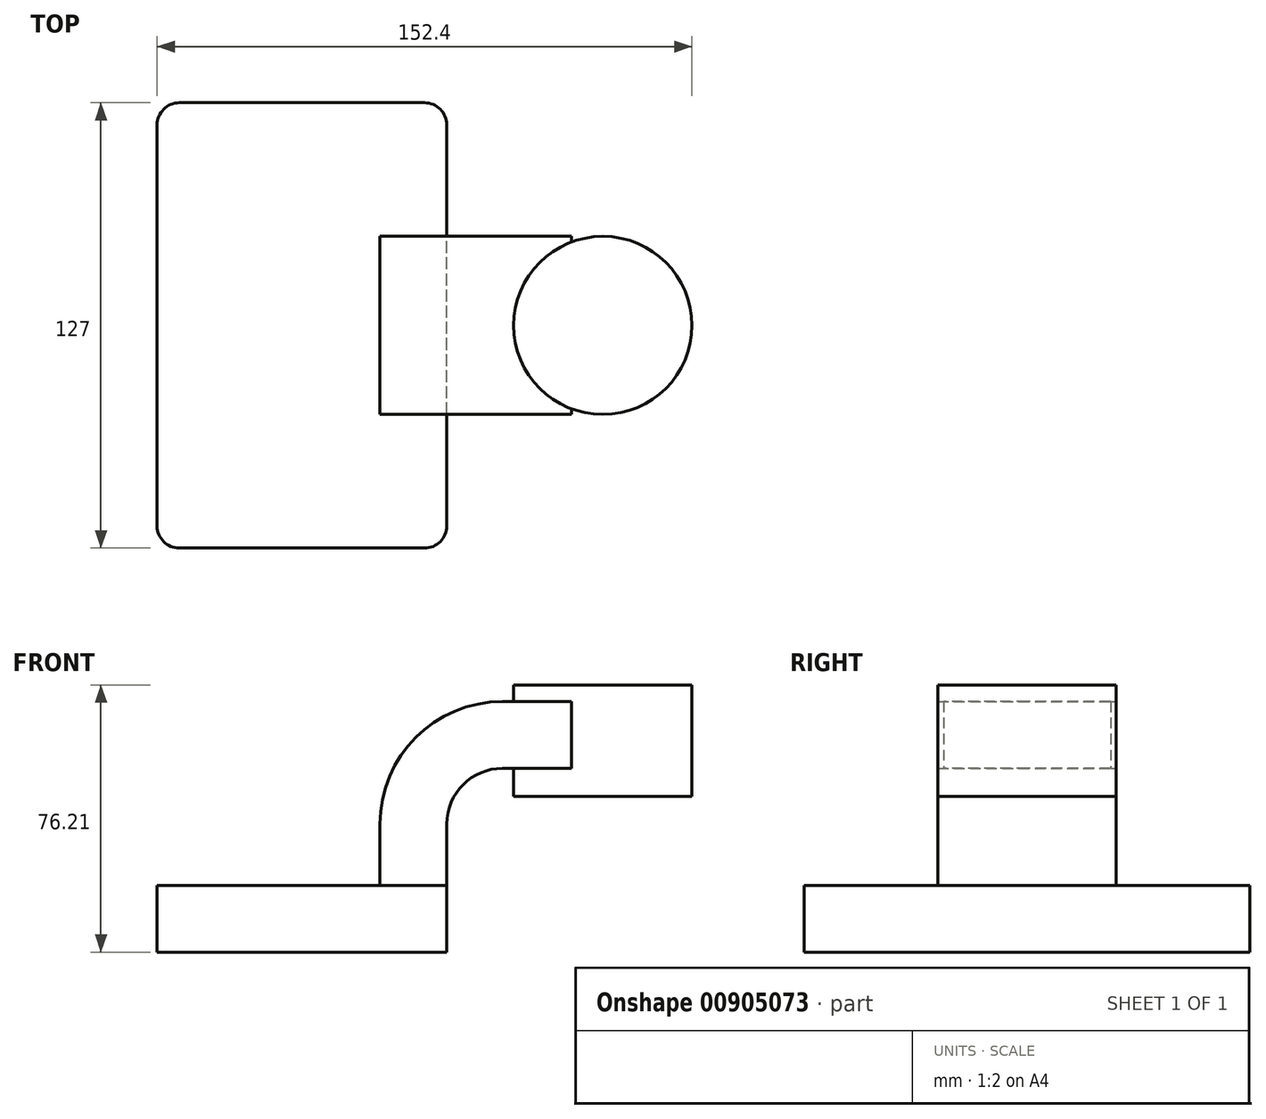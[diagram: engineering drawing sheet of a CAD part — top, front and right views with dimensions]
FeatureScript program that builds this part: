
annotation { "Feature Type Name" : "Feature", "Feature Type Description" : "" }
export const myFeature = defineFeature(function(context is Context, id is Id, definition is map)
    precondition{}
    {
        {
            var Q0;
            Q0=qCreatedBy(makeId("Front.planeOp"),FACE);
            var sketch = newSketch(context, id + "F0", { "sketchPlane" : qUnion([Q0])});
            skLineSegment(sketch, "E0.bottom", {"start": v(-41.28, -9.53) * mm, "end": v(41.28, -9.53) * mm});
            skLineSegment(sketch, "E0.top", {"start": v(-41.28, 9.53) * mm, "end": v(41.28, 9.53) * mm});
            skLineSegment(sketch, "E0.left", {"start": v(-41.28, -9.53) * mm, "end": v(-41.28, 9.53) * mm});
            skLineSegment(sketch, "E0.right", {"start": v(41.28, -9.53) * mm, "end": v(41.28, 9.52) * mm});
            skPoint(sketch, "E0.middle", {"position": v(0, 0) * mm});
            skLineSegment(sketch, "E1.bottom", {"start": v(60.33, 34.93) * mm, "end": v(111.12, 34.93) * mm});
            skLineSegment(sketch, "E1.top", {"start": v(60.32, 66.67) * mm, "end": v(111.12, 66.67) * mm});
            skLineSegment(sketch, "E1.left", {"start": v(60.33, 34.93) * mm, "end": v(60.32, 66.68) * mm});
            skLineSegment(sketch, "E1.right", {"start": v(111.12, 34.93) * mm, "end": v(111.12, 66.68) * mm});
            skPoint(sketch, "E1.middle", {"position": v(85.72, 50.8) * mm});
            skLineSegment(sketch, "E2", {"start": v(41.28, 9.52) * mm, "end": v(41.28, 27) * mm});
            skArc(sketch, "E3", {"start": v(41.27, 27) * mm, "mid": v(45.92, 38.23) * mm, "end": v(57.15, 42.88) * mm});
            skLineSegment(sketch, "E4", {"start": v(57.15, 42.88) * mm, "end": v(76.86, 42.88) * mm});
            skLineSegment(sketch, "E5.0", {"start": v(57.15, 61.93) * mm, "end": v(76.86, 61.93) * mm});
            skArc(sketch, "E5.1", {"start": v(22.23, 27) * mm, "mid": v(32.45, 51.7) * mm, "end": v(57.15, 61.93) * mm});
            skLineSegment(sketch, "E5.2", {"start": v(22.22, 9.52) * mm, "end": v(22.22, 27) * mm});
            skLineSegment(sketch, "E6", {"start": v(76.86, 42.88) * mm, "end": v(76.86, 61.93) * mm});
            skFitSpline(sketch, "E7", {"points": [v(-41.28, 9.53) * mm, v(57.15, 61.93) * mm], "startDerivative": vector(2.94, 91.77) * mm, "endDerivative": vector(171.45, -0.05) * mm});
            skLineSegment(sketch, "E8", {"start": v(85.72, 34.93) * mm, "end": v(85.72, 66.67) * mm});
            skSolve(sketch);
        }
        {
            var Q0;
            Q0=makeQuery(id+"F0.imprint","IMPRINT",FACE,{"disambiguationData":[TD([[makeQuery(id+"F0.imprint","IMPRINT",EDGE,{"derivedFrom":sQuery(id+"F0.wireOp",EDGE,"E0.bottom")}),1.0]])]});
            extrude(context, id + "F1", {"entities" : qUnion([Q0]), "endBound" : BoundingType.SYMMETRIC, "depth" : 127 * mm, "offsetDistance" : 25.4 * mm});
        }
        {
            var Q0;
            {var subQ0=sQuery(id+"F0.wireOp",EDGE,"E2");Q0=makeQuery(id+"F0.imprint","IMPRINT",FACE,{"disambiguationData":[TD([[makeQuery(id+"F0.imprint","IMPRINT",EDGE,{"derivedFrom":subQ0}),1.0]])]});}
            var Q1;
            {var subQ5=sQuery(id+"F0.wireOp",EDGE,"E6");Q1=makeQuery(id+"F0.imprint","IMPRINT",FACE,{"disambiguationData":[TD([[makeQuery(id+"F0.imprint","IMPRINT",EDGE,{"derivedFrom":subQ5}),1.0]])]});}
            extrude(context, id + "F2", {"entities" : qUnion([Q0, Q1]), "endBound" : BoundingType.SYMMETRIC, "depth" : 50.8 * mm, "offsetDistance" : 25.4 * mm});
        }
        {
            var Q0;
            Q0=makeQuery(id+"F0.imprint","IMPRINT",FACE,{"disambiguationData":[TD([[makeQuery(id+"F0.imprint","IMPRINT",EDGE,{"derivedFrom":sQuery(id+"F0.wireOp",EDGE,"E5.1")}),1.0]])]});
            extrude(context, id + "F3", {"entities" : qUnion([Q0]), "endBound" : BoundingType.SYMMETRIC, "depth" : 15.88 * mm, "offsetDistance" : 25.4 * mm});
        }
        {
            var Q0;
            {var subQ0=sQuery(id+"F0.wireOp",EDGE,"E1.right");Q0=makeQuery(id+"F0.imprint","IMPRINT",FACE,{"disambiguationData":[TD([[makeQuery(id+"F0.imprint","IMPRINT",EDGE,{"derivedFrom":subQ0}),1.0]])]});}
            var Q1;
            Q1=sQuery(id+"F0.wireOp",EDGE,"E8");
            revolve(context, id + "F4", {"operationType" : NewBodyOperationType.ADD, "surfaceOperationType" : NewSurfaceOperationType.NEW, "entities" : qUnion([Q0]), "axis" : qUnion([Q1]), "revolveType" : RevolveType.FULL});
        }
        {
            var Q0;
            Q0=makeQuery(id+"F1.opExtrude","CAP_EDGE",EDGE,{"disambiguationData":[OSD([sQuery(id+"F0.wireOp",EDGE,"E0.left")])],"isStart":false});
            var Q1;
            Q1=makeQuery(id+"F1.opExtrude","CAP_EDGE",EDGE,{"disambiguationData":[OSD([sQuery(id+"F0.wireOp",EDGE,"E0.right")])],"isStart":false});
            var Q2;
            Q2=makeQuery(id+"F1.opExtrude","CAP_EDGE",EDGE,{"disambiguationData":[OSD([sQuery(id+"F0.wireOp",EDGE,"E0.right")])],"isStart":true});
            var Q3;
            Q3=makeQuery(id+"F1.opExtrude","CAP_EDGE",EDGE,{"disambiguationData":[OSD([sQuery(id+"F0.wireOp",EDGE,"E0.left")])],"isStart":true});
            fillet(context, id + "F5", {"entities" : qUnion([Q0, Q1, Q2, Q3]), "radius" : 6.35 * mm, "tangentPropagation" : true, "allowEdgeOverflow" : false});
        }
    });
